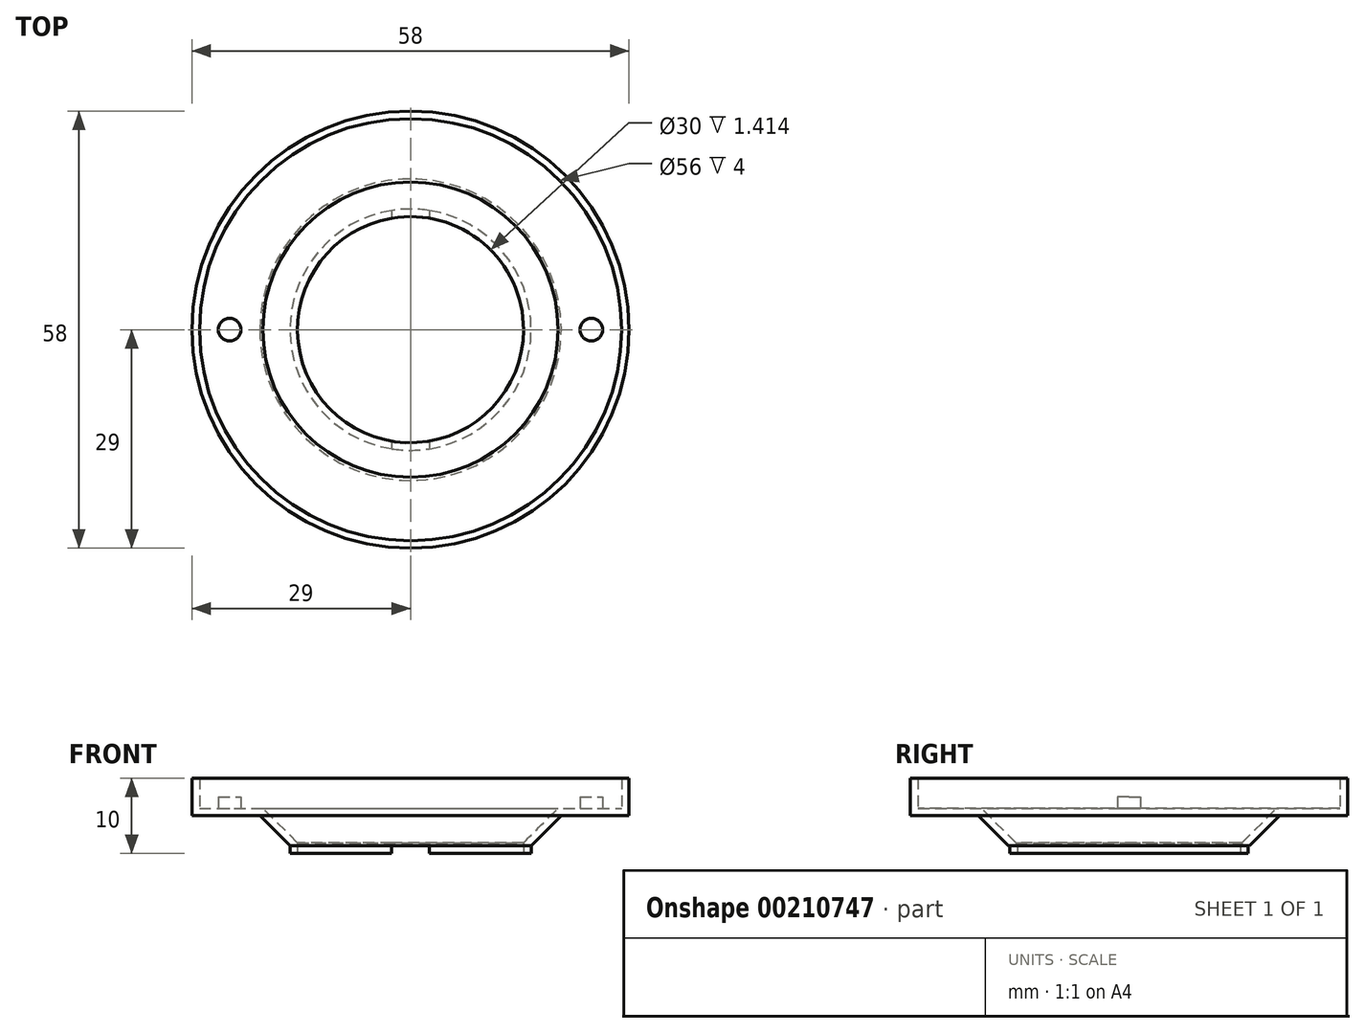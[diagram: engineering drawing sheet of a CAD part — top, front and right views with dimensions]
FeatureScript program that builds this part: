
annotation { "Feature Type Name" : "Feature", "Feature Type Description" : "" }
export const myFeature = defineFeature(function(context is Context, id is Id, definition is map)
    precondition{}
    {
        {
            var Q0;
            Q0=qCreatedBy(makeId("Top.planeOp"),FACE);
            var sketch = newSketch(context, id + "F0", { "sketchPlane" : qUnion([Q0])});
            skCircle(sketch, "E0", {"center": v(0, 0) * mm, "radius": 29 * mm});
            skSolve(sketch);
        }
        {
            var Q0;
            Q0 = qSketchRegion(id + "F0", true);
            extrude(context, id + "F1", {"entities" : qUnion([Q0]), "depth" : 10 * mm});
        }
        {
            var Q0;
            Q0=makeQuery(id+"F1.opExtrude","CAP_FACE",FACE,{"disambiguationData":[OSD([sQuery(id+"F0.wireOp",EDGE,"E0")])],"isStart":true});
            var sketch = newSketch(context, id + "F2", { "sketchPlane" : qUnion([Q0])});
            skCircle(sketch, "E1", {"center": v(0, 0) * mm, "radius": 16 * mm});
            skCircle(sketch, "E2", {"center": v(0, 0) * mm, "radius": 29 * mm});
            skSolve(sketch);
        }
        {
            var Q0;
            Q0 = qSketchRegion(id + "F2", true);
            extrude(context, id + "F3", {"entities" : qUnion([Q0]), "operationType" : NewBodyOperationType.REMOVE, "oppositeDirection" : true, "depth" : 5 * mm});
        }
        {
            var Q0;
            Q0=makeQuery(id+"F3.boolean.opBoolean","COPY",EDGE,{"derivedFrom":makeQuery(id+"F3.opExtrude","CAP_EDGE",EDGE,{"disambiguationData":[OSD([sQuery(id+"F2.wireOp",EDGE,"E1")])],"isStart":false})});
            chamfer(context, id + "F4", {"entities" : qUnion([Q0]), "width" : 4 * mm, "tangentPropagation" : true});
        }
        {
            var Q0;
            Q0=makeQuery(id+"F1.opExtrude","CAP_FACE",FACE,{"disambiguationData":[OSD([sQuery(id+"F0.wireOp",EDGE,"E0")])],"isStart":false});
            var Q1;
            Q1=makeQuery(id+"F1.opExtrude","CAP_FACE",FACE,{"disambiguationData":[OSD([sQuery(id+"F0.wireOp",EDGE,"E0")])],"isStart":true});
            shell(context, id + "F5", {"entities" : qUnion([Q0, Q1]), "thickness" : 1 * mm});
        }
        {
            var Q0;
            Q0=makeQuery(id+"F5.opShell","OFFSET_FACE",FACE,{"disambiguationData":[OSD([sQuery(id+"F2.wireOp",EDGE,"E1"),sQuery(id+"F2.wireOp",EDGE,"E2")])]});
            var sketch = newSketch(context, id + "F6", { "sketchPlane" : qUnion([Q0])});
            skCircle(sketch, "E3", {"center": v(-24, 0) * mm, "radius": 1.5 * mm});
            skCircle(sketch, "E4", {"center": v(24, 0) * mm, "radius": 1.5 * mm});
            skLineSegment(sketch, "E5", {"start": v(-24, 0) * mm, "end": v(24, 0) * mm, "construction": true});
            skSolve(sketch);
        }
        {
            var Q0;
            Q0 = qSketchRegion(id + "F6", true);
            extrude(context, id + "F7", {"entities" : qUnion([Q0]), "operationType" : NewBodyOperationType.ADD, "depth" : 1.5 * mm});
        }
        {
            var Q0;
            Q0=qCreatedBy(makeId("Front.planeOp"),FACE);
            var sketch = newSketch(context, id + "F8", { "sketchPlane" : qUnion([Q0])});
            skLineSegment(sketch, "E6.bottom", {"start": v(-2.5, 0) * mm, "end": v(2.5, 0) * mm});
            skLineSegment(sketch, "E6.top", {"start": v(-2.5, 1) * mm, "end": v(2.5, 1) * mm});
            skLineSegment(sketch, "E6.left", {"start": v(-2.5, 0) * mm, "end": v(-2.5, 1) * mm});
            skLineSegment(sketch, "E6.right", {"start": v(2.5, 0) * mm, "end": v(2.5, 1) * mm});
            skSolve(sketch);
        }
        {
            var Q0;
            Q0 = qSketchRegion(id + "F8", true);
            extrude(context, id + "F9", {"entities" : qUnion([Q0]), "operationType" : NewBodyOperationType.REMOVE, "endBound" : BoundingType.THROUGH_ALL, "oppositeDirection" : true, "depth" : 25 * mm, "hasSecondDirection" : true, "secondDirectionBound" : SecondDirectionBoundingType.THROUGH_ALL, "secondDirectionOppositeDirection" : false, "secondDirectionDepth" : 25 * mm});
        }
    });
